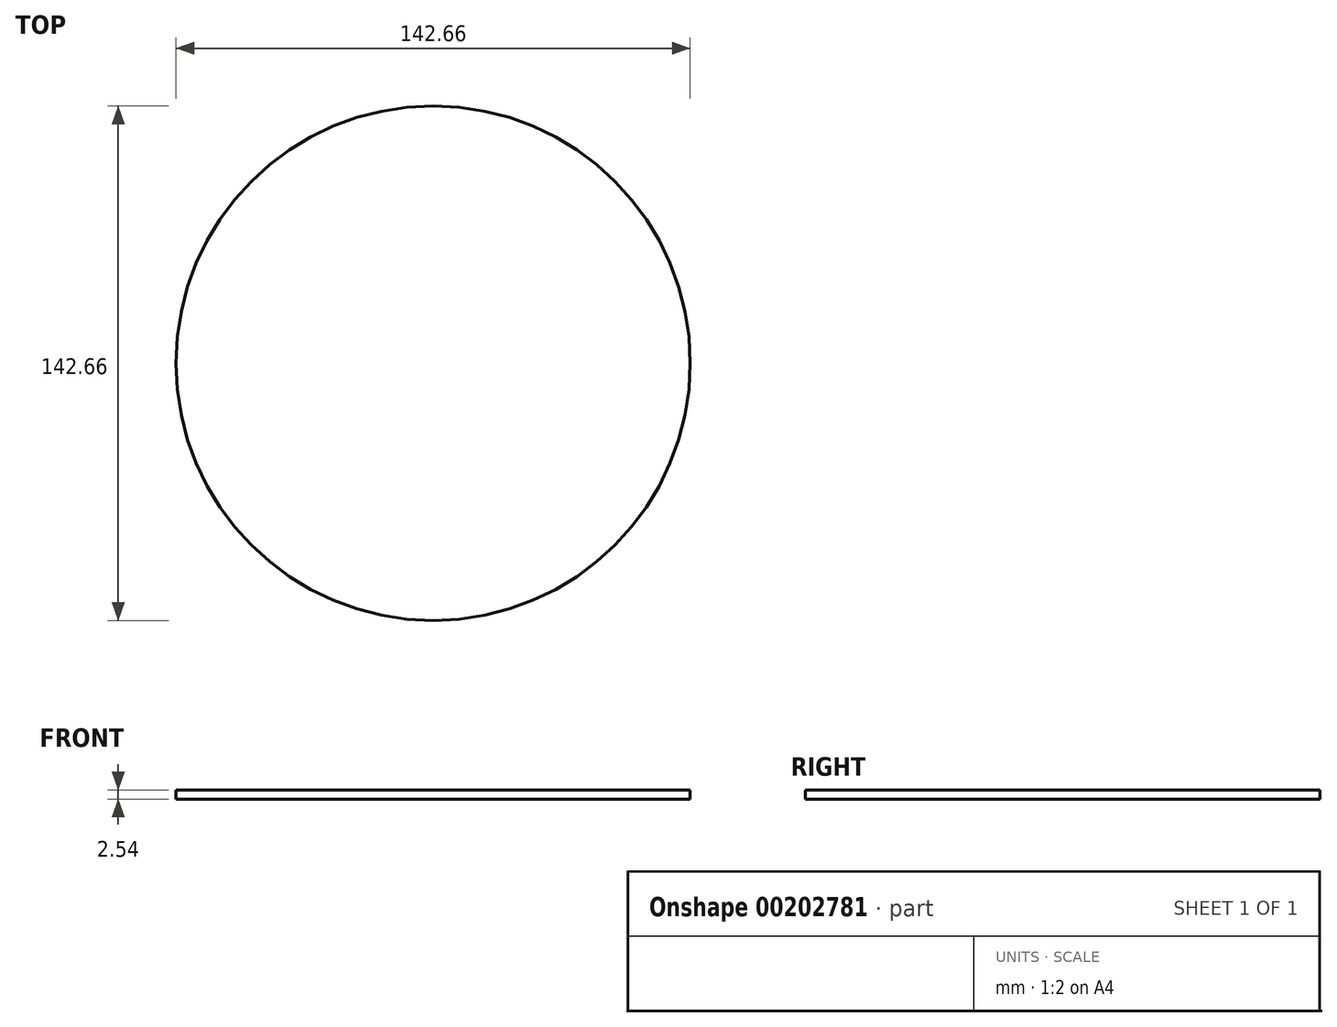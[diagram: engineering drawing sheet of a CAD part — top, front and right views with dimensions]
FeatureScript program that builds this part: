
annotation { "Feature Type Name" : "Feature", "Feature Type Description" : "" }
export const myFeature = defineFeature(function(context is Context, id is Id, definition is map)
    precondition{}
    {
        {
            var Q0;
            Q0=qCreatedBy(makeId("Top.planeOp"),FACE);
            var sketch = newSketch(context, id + "F0", { "sketchPlane" : qUnion([Q0])});
            skCircle(sketch, "E0", {"center": v(0, 0) * mm, "radius": 71.33 * mm});
            skSolve(sketch);
        }
        {
            var Q0;
            Q0=makeQuery(id+"F0.imprint","IMPRINT",FACE,{"disambiguationData":[TD([[makeQuery(id+"F0.imprint","IMPRINT",EDGE,{"derivedFrom":sQuery(id+"F0.wireOp",EDGE,"E0")}),1.0]])]});
            extrude(context, id + "F1", {"entities" : qUnion([Q0]), "depth" : 2.54 * mm});
        }
    });
